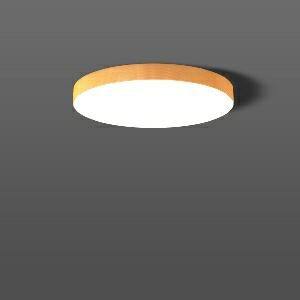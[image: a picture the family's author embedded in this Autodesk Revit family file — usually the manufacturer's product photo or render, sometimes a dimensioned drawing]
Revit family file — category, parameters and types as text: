
# Revit family: flatliner_slim_312280_002_1_8fc6
name_source: partatom
category: Lighting Fixtures
units: mm (PartAtom-declared; Revit-internal decimal feet)

## family parameters
Cut with Voids When Loaded = No
Host = Face
Light Source = No
Part Type = Normal
Room Calculation Point = No
Round Connector Dimension = Use Diameter
Shared = No

## types (1)
- 982555.002 (1 x LED Modul 840, 1050 lm, 4000)
    Apparent Load = 13 VA
    CIE Flux Codes = 45 76 94 95 100
    Color Rendering = 80
    Color Temperature = 4000
    Default Elevation = 1800 mm
    Description = Series: FLATLINER SLIM
Decorative ceiling luminaire for interior decoration. Base luminaire prepared for the installation of fabric lampshade. Base: metal, white, powder-coated. Modular design: with the basic luminaire, a cylindrical fabric lampshade with a polycarbonate satin-finish diffuser must always be ordered separately. Fabric lampshade and diffuser can be assembled without the use of tools. 
Colour: white
Diameter: 255 mm
Height: 34 mm
Lamp: LED exchangeable
Socket: without socket
Colour temperature: 4000K
Colour rendering index (CRI): 80
System power: 11 W
Rated luminous flux: 1050 lm
Beam angle Down: 117°
Luminous efficiency: 95 lm/W
Control gear: AC Strom, dim.Ph.an-/abschnitt
Protection class: I
Type of protection: IP 20
    Height = 34 mm  [stored 0.111549 ft]
    Lamp = 1 x LED Modul 840
    Lamp Light Flux = 1050 lm
    Lamp count = 1
    Length = 255 mm
    Lifetime = 50000 h
    Luminous efficacy = 81 lm/W
    Manufacturer = RZB
    ModVariant = No
    Model = 312280.002.1
    Mounting Place = Ceiling
    Mounting Type = Surface mounted
    Number of Poles = 1
    OnlyDefault = Yes
    Power Factor = 1
    Product Name = FLATLINER SLIM
    Product group = Surface mounted ceiling Fabric lampshade luminaires
    ProductGroupID = 313
    Protection Class = Protection class I
    Protection Degree = IP 20
    RLX_Detail_Level = 1
    RLX_Emergency_Light_Flux = 0 lm
    RLX_Emergency_Type = 0
    RLX_Emergency_Type_DB = No
    RlxData = <blob elided: 25313 chars, md5=d51b963a>
    Socket = socket
    Standby Power = 0 W
    System Light Flux = 1050 lm
    System Power = 13 W
    Type Image = 312287.002_982442.0063_982444.002.jpg
    URL = http://relux.com
    VarID = 982555_002_56de
    Voltage = 230 V
    Voltage Range = 220-240 V
    Weight = 0.00 kg
    Width = 0 mm  [stored 0 ft]

note: [stored X ft] marks values corroborated as IEEE doubles in the binary element streams (Revit-internal decimal feet)

## geometry (parser evidence)
native form markers: Blend x4, Sweep x11
no freeform markers — native parametric forms only
